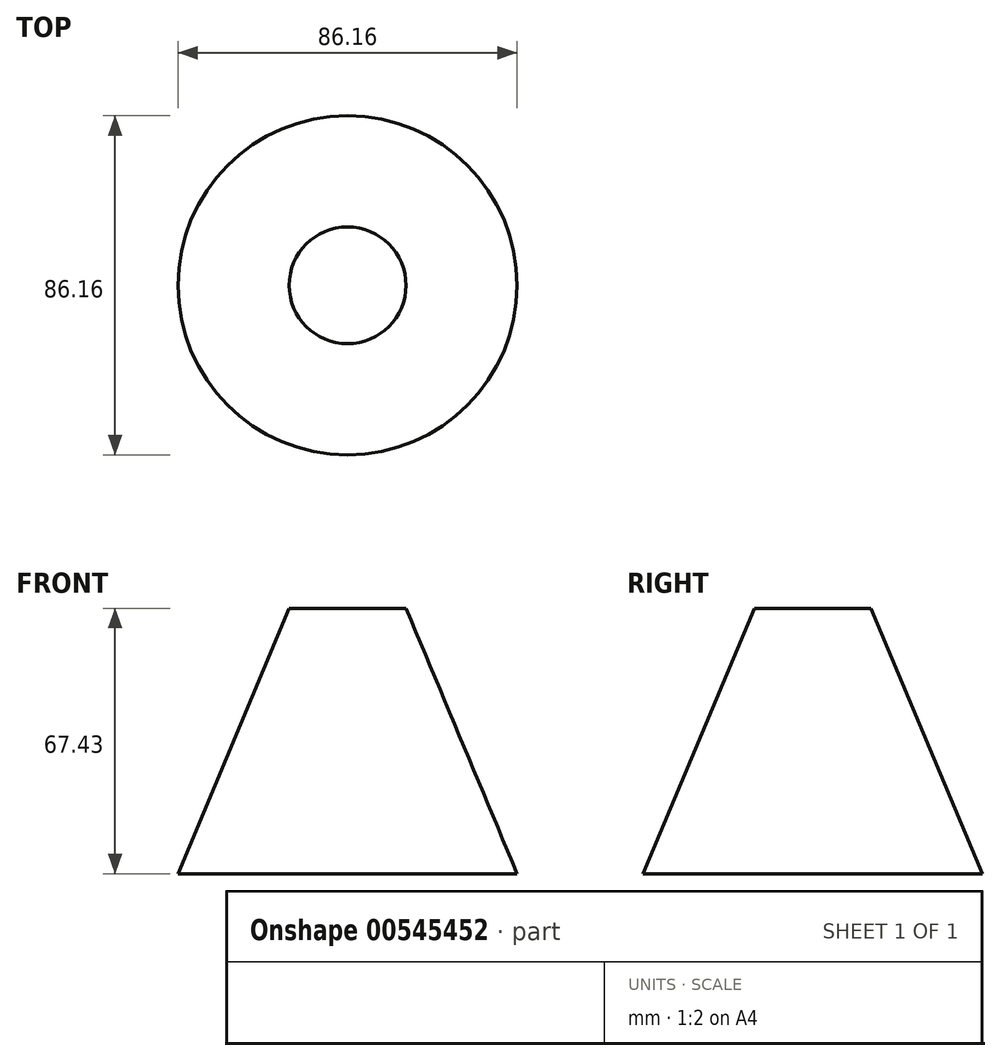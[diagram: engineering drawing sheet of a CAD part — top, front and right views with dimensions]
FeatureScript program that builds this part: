
annotation { "Feature Type Name" : "Feature", "Feature Type Description" : "" }
export const myFeature = defineFeature(function(context is Context, id is Id, definition is map)
    precondition{}
    {
        {
            var Q0;
            Q0=qCreatedBy(makeId("Front.planeOp"),FACE);
            var sketch = newSketch(context, id + "F0", { "sketchPlane" : qUnion([Q0])});
            skLineSegment(sketch, "E0", {"start": v(0, 0) * mm, "end": v(43.08, 0) * mm});
            skLineSegment(sketch, "E1", {"start": v(43.08, 0) * mm, "end": v(14.84, 67.43) * mm});
            skLineSegment(sketch, "E2", {"start": v(0, 67.43) * mm, "end": v(0, 0) * mm});
            skLineSegment(sketch, "E3", {"start": v(0, 67.43) * mm, "end": v(14.84, 67.43) * mm});
            skPoint(sketch, "E4.orphan", {"position": v(0, 102.88) * mm});
            skSolve(sketch);
        }
        {
            var Q0;
            Q0=makeQuery(id+"F0.imprint","IMPRINT",FACE,{"disambiguationData":[TD([[makeQuery(id+"F0.imprint","IMPRINT",EDGE,{"derivedFrom":sQuery(id+"F0.wireOp",EDGE,"E0")}),1.0]])]});
            var Q1;
            Q1=sQuery(id+"F0.wireOp",EDGE,"E2");
            revolve(context, id + "F1", {"entities" : qUnion([Q0]), "axis" : qUnion([Q1]), "revolveType" : RevolveType.FULL});
        }
    });
